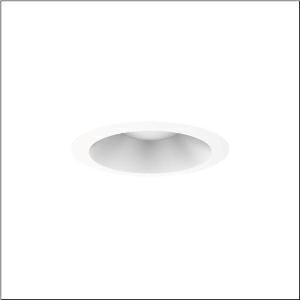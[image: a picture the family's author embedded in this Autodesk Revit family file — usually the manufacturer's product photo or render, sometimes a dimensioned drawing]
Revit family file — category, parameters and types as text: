
# Revit family: lunis_31_midi_51dn167g42
name_source: partatom
category: Lighting Fixtures
units: mm (PartAtom-declared; Revit-internal decimal feet)

## family parameters
Cut with Voids When Loaded = No
Host = Face
Light Source = No
Part Type = Normal
Room Calculation Point = No
Round Connector Dimension = Use Diameter
Shared = No

## types (1)
- Lunis 31 midi (1 x LED, 2150 lm, 17 W, 4000K)
    Apparent Load = 17 VA
    CIE Flux Codes = 64 93 99 100 100
    Color Rendering = 80
    Color Temperature = 4000K
    Default Elevation = 1800 mm
    Description = Lunis 31,  midi, downlight, light control with reflector, light emission: direct distribution, LED rated luminous flux: 2.150lm, light colour: 840, mains connection: 220..240V, AC, 50/60Hz, housing, white, protection rating (complete): IP20, protection rating (on room side): IP54, insulation class (complete): insulation class II (safety insulation), certification: CE, packaging unit: 1 piece
    Height = 0 mm  [stored 0 ft]
    Lamp = 1 x LED
    Lamp Light Flux = 2150 lm
    Lamp Power = 17 W
    Lamp count = 1
    Length = 259 mm
    Luminous efficacy = 126 lm/W
    Manufacturer = Siteco
    ModVariant = No
    Model = 51DN167G42
    Mounting Place = Ceiling
    Mounting Type = Recessed
    Number of Poles = 1
    OnlyDefault = Yes
    Power Factor = 1
    Product Name = Lunis 31 midi
    Product group = downlight
    ProductGroupID = 400
    Protection Class = Protection class II
    Protection Degree = IP 20
    RLX_Detail_Level = 1
    RLX_Emergency_Light_Flux = 0 lm
    RLX_Emergency_Type = 0
    RLX_Emergency_Type_DB = No
    RlxData = <blob elided: 23741 chars, md5=45dc64b2>
    Socket = socket
    Standby Power = 0 W
    System Light Flux = 2150 lm
    System Power = 17 W
    Type Comments = Product without accessories
    Type Image = l_1006711.jpg
    URL = http://relux.com
    VarID = ---
    Voltage = 0 V
    Weight = 0.00 kg
    Width = 0 mm  [stored 0 ft]

note: [stored X ft] marks values corroborated as IEEE doubles in the binary element streams (Revit-internal decimal feet)

## geometry (parser evidence)
native form markers: Blend x4, Sweep x10
no freeform markers — native parametric forms only
